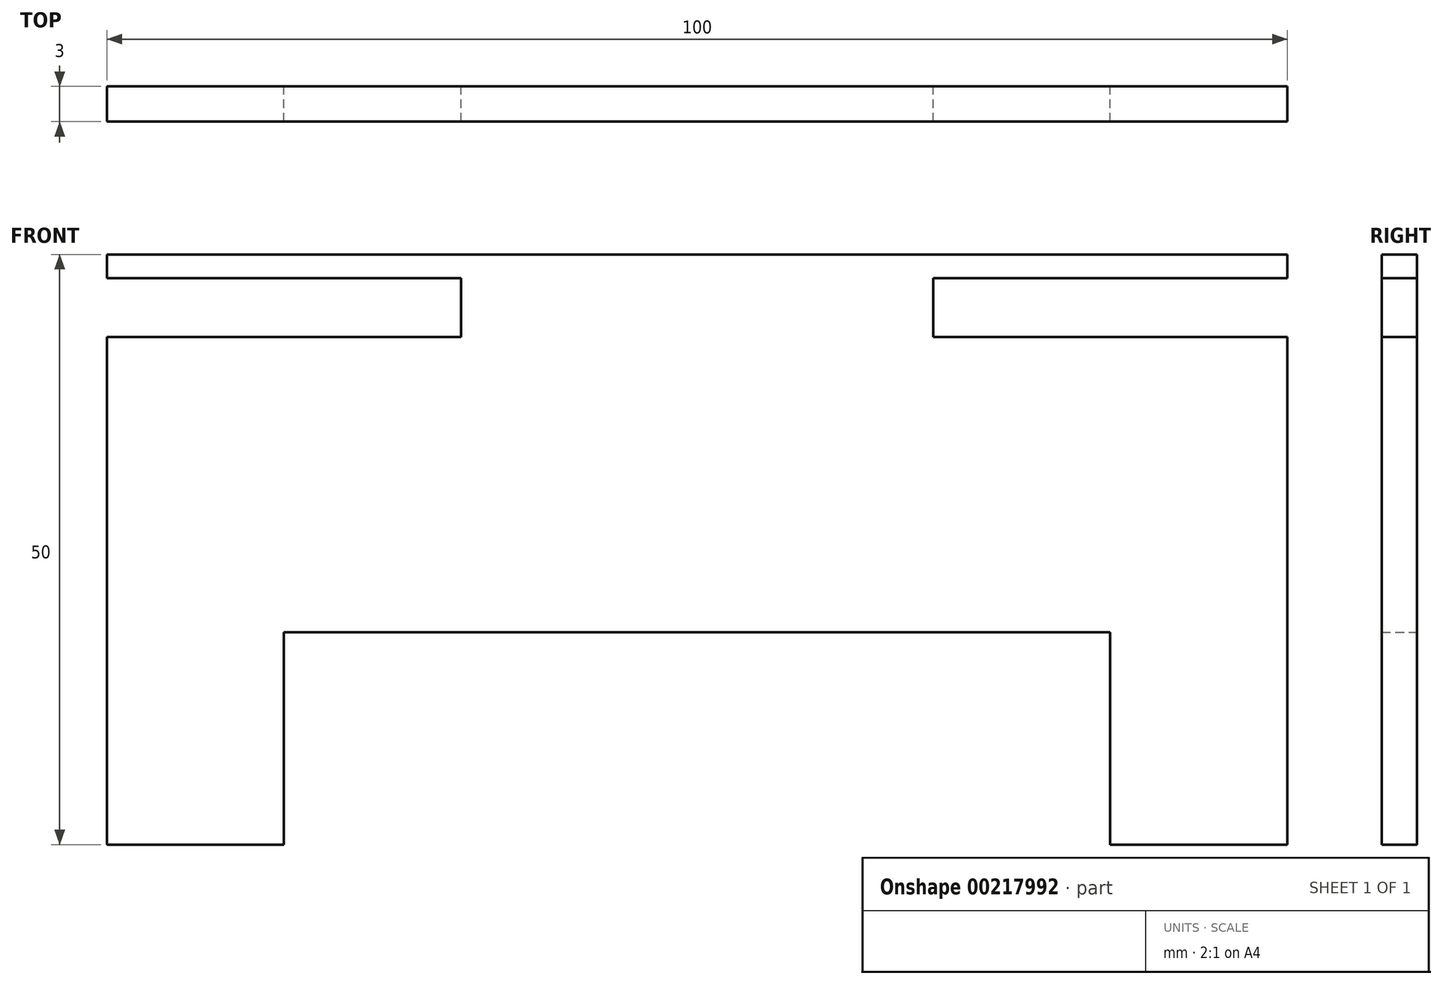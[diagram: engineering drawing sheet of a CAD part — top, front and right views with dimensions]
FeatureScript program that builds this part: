
annotation { "Feature Type Name" : "Feature", "Feature Type Description" : "" }
export const myFeature = defineFeature(function(context is Context, id is Id, definition is map)
    precondition{}
    {
        {
            var Q0;
            Q0=qCreatedBy(makeId("Front.planeOp"),FACE);
            var sketch = newSketch(context, id + "F0", { "sketchPlane" : qUnion([Q0])});
            skLineSegment(sketch, "E0", {"start": v(-50.93, 32) * mm, "end": v(49.07, 32) * mm});
            skLineSegment(sketch, "E1", {"start": v(49.07, -18) * mm, "end": v(34.07, -18) * mm});
            skLineSegment(sketch, "E2", {"start": v(34.07, -18) * mm, "end": v(34.07, 0) * mm});
            skLineSegment(sketch, "E3", {"start": v(34.07, 0) * mm, "end": v(-35.93, 0) * mm});
            skLineSegment(sketch, "E4", {"start": v(-35.93, 0) * mm, "end": v(-35.93, -18) * mm});
            skLineSegment(sketch, "E5", {"start": v(-35.93, -18) * mm, "end": v(-50.93, -18) * mm});
            skLineSegment(sketch, "E6.bottom", {"start": v(49.07, 30) * mm, "end": v(19.07, 30) * mm});
            skLineSegment(sketch, "E6.top", {"start": v(49.07, 25) * mm, "end": v(19.07, 25) * mm});
            skLineSegment(sketch, "E6.right", {"start": v(19.07, 30) * mm, "end": v(19.07, 25) * mm});
            skLineSegment(sketch, "E7.bottom", {"start": v(-50.93, 30) * mm, "end": v(-20.93, 30) * mm});
            skLineSegment(sketch, "E7.top", {"start": v(-50.93, 25) * mm, "end": v(-20.93, 25) * mm});
            skLineSegment(sketch, "E7.right", {"start": v(-20.93, 30) * mm, "end": v(-20.93, 25) * mm});
            skLineSegment(sketch, "E8", {"start": v(-50.93, 32) * mm, "end": v(-50.93, 30) * mm});
            skLineSegment(sketch, "E9", {"start": v(-50.93, 25) * mm, "end": v(-50.93, -18) * mm});
            skLineSegment(sketch, "E10", {"start": v(49.07, 30) * mm, "end": v(49.07, 32) * mm});
            skLineSegment(sketch, "E11", {"start": v(49.07, 25) * mm, "end": v(49.07, -18) * mm});
            skSolve(sketch);
        }
        {
            var Q0;
            Q0=qSketchRegion(id+"F0",true);
            extrude(context, id + "F1", {"entities" : qUnion([Q0]), "depth" : 3 * mm});
        }
    });
